# Revit family: HCS_NXSW-CCT
name_source: partatom
category: Communication Devices
units: mm (PartAtom-declared; Revit-internal decimal feet)

## family parameters
Cut with Voids When Loaded = No
Host = Face
Maintain Annotation Orientation = No
OmniClass Number = 23.85.80.11.27
OmniClass Title = Lighting Controls
Part Type = Normal
Room Calculation Point = No
Round Connector Dimension = Use Diameter
Shared = Yes

## types (1)
- HCS_NXSW-CCT
    Assembly Code = D5090
    Black = Paint - Carbon Black
    Blue = Plastic -  Blue
    Default Elevation = 48 "
    Description = The NXSW-CCT switch provides chromaticity control of SpectraSync™ tunable white enabled luminaires.The NXSW-CCT switch is provided with four color temperature preset buttons which allows the user to select between four preset tunable white settings.
    Features = Compatible with  Lighting’s SpectraSync enabled luminaires
• Attractive, decorator style design
• Mounts to standard single or multi-gang switch box
• Four factory preset LED color selections
• Manual raise to cool and lower to warm buttons
• Plug and Play integration with NX control system
• Simple CAT5 connection
• Five year limited warranty
• Class 2, low voltage device, 24 VDC
    Manufacturer = NX Lighting Controls
    Model = NX CCT Switch Station
    Type Comments = NX CCT Switch Station
    URL = https://www.currentlighting.com
    Warranty = 5-Years Warranty
    White = Paint - Matte White
    Yellow = Plastic -  Yellow

## geometry (parser evidence)
native form markers: Sweep x2
no freeform markers — native parametric forms only
